# Revit family: Camera-Security-Panasonic-Dome-Super_Dynamic-Vandal_Resistant-Network-SFV130x
name_source: partatom
category: Security Devices
revit_build: Autodesk Revit 2013 (Build: 20130531_2115(x64)
units: mm (PartAtom-declared; Revit-internal decimal feet)

## types (4) — shared parameters
Audio In = No
Audio Out = No
Date Last Modified = May, 31, 2016
Day Or Night = Yes
Diameter = 4.281 "
Dome Part Number = WV-CW6SA
Equipment Abbreviation = SC
Family Version = 1.0.0
Has POE = Yes
Height = 1.844 "
IP Or Analog = IP
Indoor Or Outdoor = Outdoor
Manufacturer = Panasonic
Minimum Illumination = 0 lx
Model Disclaimer = Contact Panasonic for more information
Mounting Positions = Mount Dependent
Operational Humidity = 10% to 90% (no condensation)
Operational Temperature = -40°F - 140°F
Panning Range = -20 to +20
Power Active = 4.3 W
Product Documentation Link = http://ssbu-t.psn-web.net
Product Material = Aluminum - Panasonic - Light Gray
Product Page URL = http://security.panasonic.com
Provide Feedback = https://www.surveymonkey.com
Regulatory Compliance = UL (UL60950-1), C-UL (CAN/CSA C22.2 No.60950-1), CE, IEC60950-1 FCC Part15 ClassA, ICES003 ClassA, EN55022 ClassB, EN55024
Storage Temperature = -40°F - 140°F
Tilt Max = 90.00°
Tilt Min = -20.00°
Tilting Range = -20 to +90
URL = http://security.panasonic.com
Vandal Resistant = Yes
Voltage AC = 0 V
Voltage DC = 48 V
Weight = 0.77 lb
Wide Dynamic Range = Yes
z Base Radius = 2.141 "
z Const Pan Handle Length = 27.559 "
z Const Tilt Base Length = 9.843 "
z Const Tilt Base2 Length = 19.685 "
z Const Tilt Handle Length = 14.173 "
z Const Yaw Base Length = 10.236 "
z Const Yaw Base2 Length = 17.323 "
z Const Yaw Handle Length = 9.252 "
z Dome Material = PC Resin - Panasonic - Clear
z VV Viewpoint Depth Max = 0.797 "
z VV Viewpoint Depth Min = 0.797 "
zero-valued in all types: Default Elevation

## per-type parameters (varying)
| type | Angle Of View | Communication Ports | Description | HFOV Max 169 | HFOV Max 43 | HFOV Min 169 | HFOV Min 43 | Part Description | VFOV Max 169 | VFOV Max 43 | VFOV Min 169 | VFOV Min 43 | z Camera Resolution Type |
| WV-SFV130 | 108 | 10Base-T / 100Base-TX, RJ45 connector | Super Dynamic Full HD Vandal Resistant Dome Network Camera, SFV130 | 108.00° | 89.00° | 108.00° | 89.00° | Super Dynamic Full HD Vandal Resistant Dome Network Camera, SFV130 | 60.00° | 66.00° | 60.00° | 66.00° | 1 |
| WV-SFV110 | 100 | 10Base-T / 100Base-TX, RJ45 connector | Super Dynamic HD Vandal Resistant Dome Network Camera, SFV110 | 100.00° | 100.00° | 100.00° | 100.00° | Super Dynamic HD Vandal Resistant Dome Network Camera, SFV110 | 55.00° | 73.00° | 55.00° | 73.00° | 2 |
| WV-SFV130M | 108 | 10Base-T / 100Base-TX, M12 connector | Super Dynamic Full HD Vandal Resistant Dome Network Camera, SFV130M | 108.00° | 89.00° | 108.00° | 89.00° | Super Dynamic Full HD Vandal Resistant Dome Network Camera, SFV130M | 60.00° | 66.00° | 60.00° | 66.00° | 1 |
| WV-SFV110M | 100 | 10Base-T / 100Base-TX, M12 connector | Super Dynamic HD Vandal Resistant Dome Network Camera, SFV110M | 100.00° | 100.00° | 100.00° | 100.00° | Super Dynamic HD Vandal Resistant Dome Network Camera, SFV110M | 55.00° | 73.00° | 55.00° | 73.00° | 2 |

note: column(s) folded — value = type name in every type: Model, Part Number

## geometry (parser evidence)
native form markers: Blend x8, Extrusion x1, Sweep x3
no freeform markers — native parametric forms only
